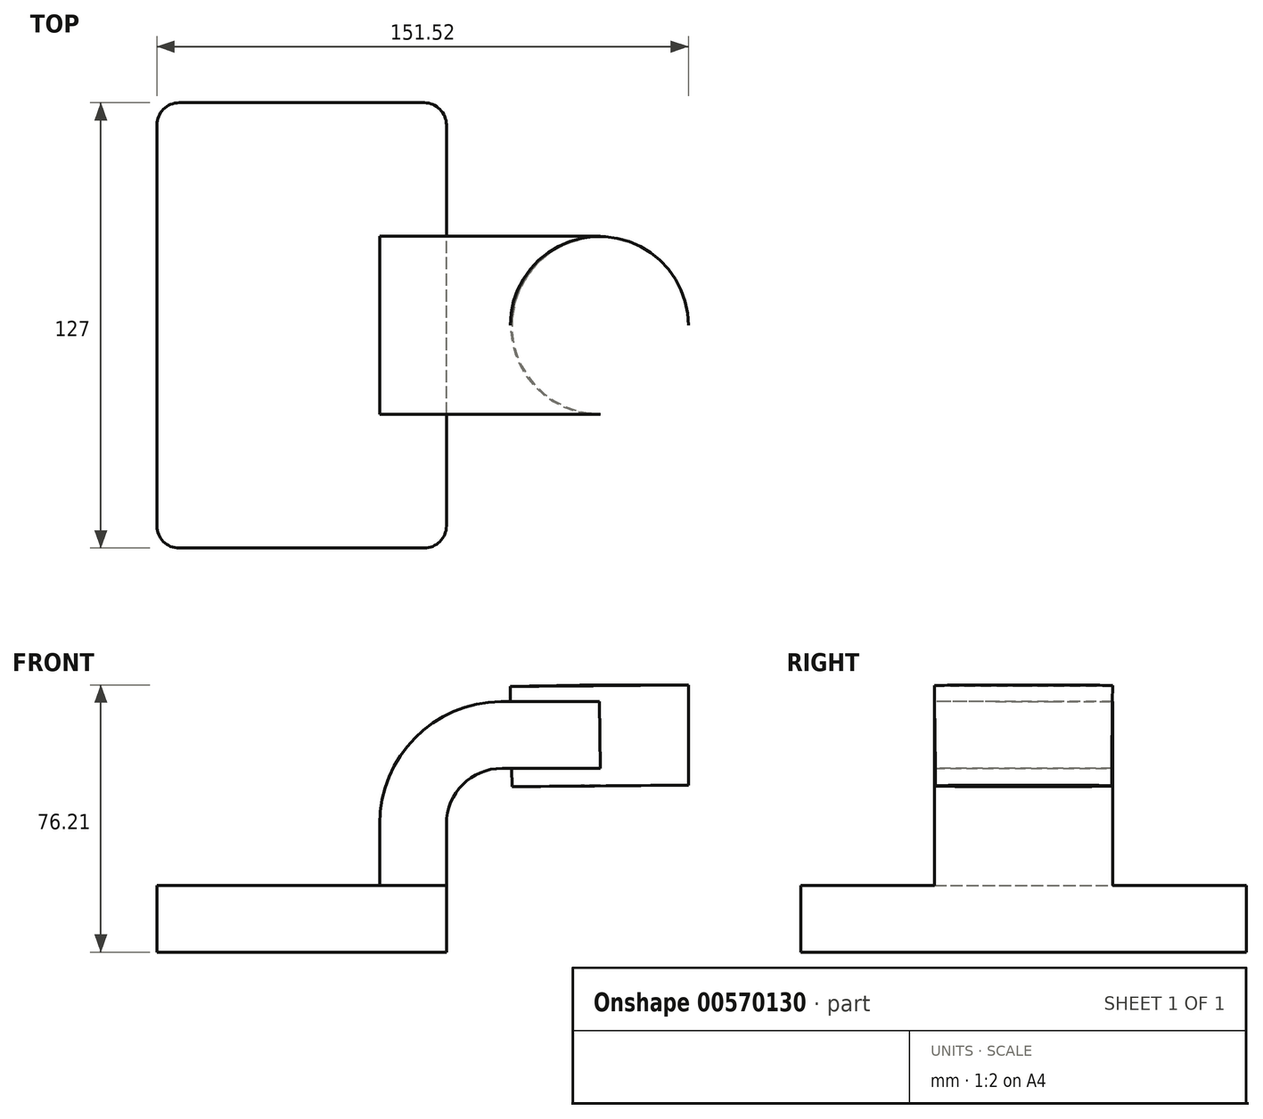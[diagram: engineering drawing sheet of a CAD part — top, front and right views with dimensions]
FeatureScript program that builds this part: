
annotation { "Feature Type Name" : "Feature", "Feature Type Description" : "" }
export const myFeature = defineFeature(function(context is Context, id is Id, definition is map)
    precondition{}
    {
        {
            var Q0;
            Q0=qCreatedBy(makeId("Front.planeOp"),FACE);
            var sketch = newSketch(context, id + "F0", { "sketchPlane" : qUnion([Q0])});
            skLineSegment(sketch, "E0.bottom", {"start": v(-41.28, -9.53) * mm, "end": v(41.28, -9.53) * mm});
            skLineSegment(sketch, "E0.top", {"start": v(-41.28, 9.53) * mm, "end": v(41.28, 9.53) * mm});
            skLineSegment(sketch, "E0.left", {"start": v(-41.28, -9.53) * mm, "end": v(-41.28, 9.53) * mm});
            skLineSegment(sketch, "E0.right", {"start": v(41.28, -9.53) * mm, "end": v(41.28, 9.53) * mm});
            skPoint(sketch, "E0.middle", {"position": v(0, 0) * mm});
            skLineSegment(sketch, "E1", {"start": v(41.28, 9.53) * mm, "end": v(41.28, 27) * mm});
            skArc(sketch, "E2", {"start": v(41.28, 27) * mm, "mid": v(45.92, 38.23) * mm, "end": v(57.15, 42.88) * mm});
            skLineSegment(sketch, "E3", {"start": v(57.15, 42.88) * mm, "end": v(85.12, 42.88) * mm});
            skLineSegment(sketch, "E4.bottom", {"start": v(110.25, 66.68) * mm, "end": v(59.45, 66.68) * mm});
            skLineSegment(sketch, "E4.top", {"start": v(110.25, 38.1) * mm, "end": v(59.45, 38.1) * mm});
            skLineSegment(sketch, "E4.left", {"start": v(110.25, 66.67) * mm, "end": v(110.25, 38.1) * mm});
            skLineSegment(sketch, "E4.right", {"start": v(59.45, 66.67) * mm, "end": v(59.45, 38.1) * mm});
            skPoint(sketch, "E4.middle", {"position": v(84.85, 52.39) * mm});
            skLineSegment(sketch, "E5.0", {"start": v(57.15, 61.93) * mm, "end": v(85.12, 61.93) * mm});
            skArc(sketch, "E5.1", {"start": v(22.23, 27) * mm, "mid": v(32.45, 51.7) * mm, "end": v(57.15, 61.93) * mm});
            skLineSegment(sketch, "E5.2", {"start": v(22.23, 9.53) * mm, "end": v(22.23, 27) * mm});
            skLineSegment(sketch, "E6", {"start": v(84.85, 66.68) * mm, "end": v(85.12, 38.1) * mm});
            skFitSpline(sketch, "E7", {"points": [v(-41.28, 9.52) * mm, v(57.15, 61.93) * mm], "startDerivative": vector(0.6, 59.26) * mm, "endDerivative": vector(128.86, 0.4) * mm});
            skSolve(sketch);
        }
        {
            var Q0;
            Q0=makeQuery(id+"F0.imprint","IMPRINT",FACE,{"disambiguationData":[TD([[makeQuery(id+"F0.imprint","IMPRINT",EDGE,{"derivedFrom":sQuery(id+"F0.wireOp",EDGE,"E0.bottom")}),1.0]])]});
            extrude(context, id + "F1", {"entities" : qUnion([Q0]), "endBound" : BoundingType.SYMMETRIC, "depth" : 127 * mm, "offsetDistance" : 25.4 * mm});
        }
        {
            var Q0;
            {var subQ6=sQuery(id+"F0.wireOp",EDGE,"E1");Q0=makeQuery(id+"F0.imprint","IMPRINT",FACE,{"disambiguationData":[TD([[makeQuery(id+"F0.imprint","IMPRINT",EDGE,{"derivedFrom":subQ6}),1.0]])]});}
            var Q1;
            {var subQ0=sQuery(id+"F0.wireOp",EDGE,"E4.right");var subQ1=sQuery(id+"F0.wireOp",EDGE,"E3");var subQ2=makeQuery(id+"F0.imprint","INTERSECT",VERTEX,{"derivedFrom":[subQ1,subQ0]});Q1=makeQuery(id+"F0.imprint","IMPRINT",FACE,{"disambiguationData":[TD([[makeQuery(id+"F0.imprint","IMPRINT",EDGE,{"disambiguationData":[TD([[subQ2,-1.0]])],"derivedFrom":subQ1}),1.0]])]});}
            extrude(context, id + "F2", {"entities" : qUnion([Q0, Q1]), "operationType" : NewBodyOperationType.ADD, "endBound" : BoundingType.SYMMETRIC, "depth" : 50.8 * mm, "offsetDistance" : 25.4 * mm});
        }
        {
            var Q0;
            {var subQ4=sQuery(id+"F0.wireOp",EDGE,"E5.1");Q0=makeQuery(id+"F0.imprint","IMPRINT",FACE,{"disambiguationData":[TD([[makeQuery(id+"F0.imprint","IMPRINT",EDGE,{"derivedFrom":subQ4}),1.0]])]});}
            extrude(context, id + "F3", {"entities" : qUnion([Q0]), "operationType" : NewBodyOperationType.ADD, "endBound" : BoundingType.SYMMETRIC, "depth" : 15.88 * mm, "offsetDistance" : 25.4 * mm});
        }
        {
            var Q0;
            {var subQ0=sQuery(id+"F0.wireOp",EDGE,"E4.left");Q0=makeQuery(id+"F0.imprint","IMPRINT",FACE,{"disambiguationData":[TD([[makeQuery(id+"F0.imprint","IMPRINT",EDGE,{"derivedFrom":subQ0}),-1.0]])]});}
            var Q1;
            Q1=sQuery(id+"F0.wireOp",EDGE,"E6");
            revolve(context, id + "F4", {"operationType" : NewBodyOperationType.ADD, "entities" : qUnion([Q0]), "axis" : qUnion([Q1]), "revolveType" : RevolveType.FULL});
        }
        {
            var Q0;
            Q0=makeQuery(id+"F1.opExtrude","CAP_EDGE",EDGE,{"disambiguationData":[OSD([sQuery(id+"F0.wireOp",EDGE,"E0.right")])],"isStart":false});
            var Q1;
            Q1=makeQuery(id+"F1.opExtrude","CAP_EDGE",EDGE,{"disambiguationData":[OSD([sQuery(id+"F0.wireOp",EDGE,"E0.left")])],"isStart":false});
            var Q2;
            Q2=makeQuery(id+"F1.opExtrude","CAP_EDGE",EDGE,{"disambiguationData":[OSD([sQuery(id+"F0.wireOp",EDGE,"E0.right")])],"isStart":true});
            var Q3;
            Q3=makeQuery(id+"F1.opExtrude","CAP_EDGE",EDGE,{"disambiguationData":[OSD([sQuery(id+"F0.wireOp",EDGE,"E0.left")])],"isStart":true});
            fillet(context, id + "F5", {"entities" : qUnion([Q0, Q1, Q2, Q3]), "radius" : 6.35 * mm, "tangentPropagation" : true, "allowEdgeOverflow" : false});
        }
    });
